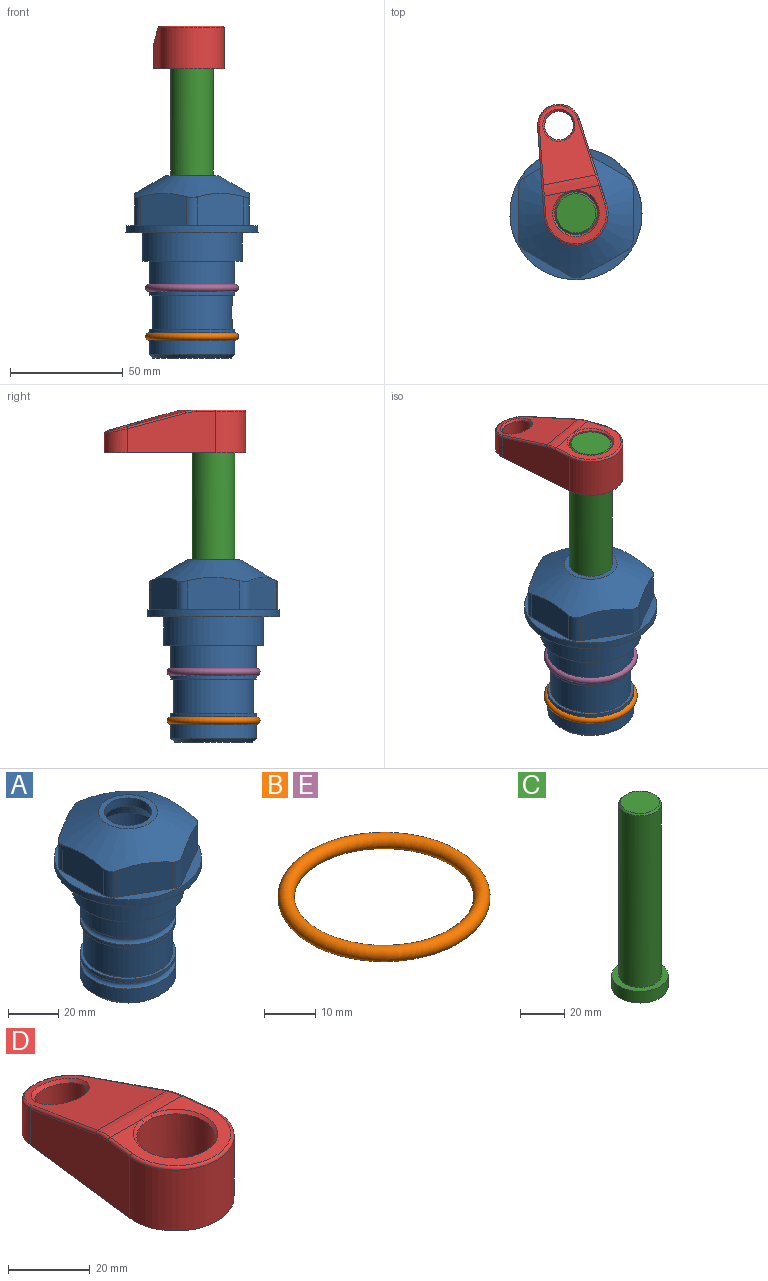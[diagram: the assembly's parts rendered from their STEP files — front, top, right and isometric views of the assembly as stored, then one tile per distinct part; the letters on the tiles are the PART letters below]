
ASSEMBLY  parts=5 mates=4
PART A: 36 faces, bbox 58.7x58.7x81 mm
  f0: cylinder r=17.78mm len=35.56mm, axis (0,0,1), area 1670.8mm2, adj f23,f24,f31
  f1: cylinder r=19.05mm len=38.1mm, axis (0,0,1), area 1191.9mm2, adj f26,f27,f30
  f2: plane 58.66x58.66mm, normal (0,0,-1), area 1150.6mm2, adj f3,f28
  f3: cylinder r=29.33mm len=58.66mm, axis (0,0,-1), area 585.1mm2, adj f2,f4
  f4: plane 58.66x58.66mm, normal (0,0,1), area 475.9mm2, adj f3,f5,f6,f7,f8,f9,f10,f11
  f5: plane 20.32x14.34mm, normal (-0.5,0.87,0), area 324.4mm2, adj f4,f15,f16,f17
  f6: plane 20.32x14.34mm, normal (0.5,0.87,0), area 324.4mm2, adj f4,f14,f15,f17
  f7: plane 23.48x14.34mm, normal (1,0,0), area 324.4mm2, adj f4,f13,f14,f17
  f8: plane 20.32x14.34mm, normal (0.5,-0.87,0), area 324.4mm2, adj f4,f12,f13,f17
  f9: plane 20.32x14.34mm, normal (-0.5,-0.87,0), area 324.4mm2, adj f4,f11,f12,f17
  f10: plane 23.48x14.34mm, normal (-1,0,0), area 324.4mm2, adj f4,f11,f16,f17
  f11: cylinder r=5.08mm len=12.85mm, axis (0,0,-1), area 67.2mm2, adj f4,f9,f10,f17
  f12: cylinder r=5.08mm len=12.85mm, axis (0,0,-1), area 67.2mm2, adj f4,f8,f9,f17
  f13: cylinder r=5.08mm len=12.85mm, axis (0,0,-1), area 67.2mm2, adj f4,f7,f8,f17
  f14: cylinder r=5.08mm len=12.85mm, axis (0,0,-1), area 67.2mm2, adj f4,f6,f7,f17
  f15: cylinder r=5.08mm len=12.85mm, axis (0,0,-1), area 67.2mm2, adj f4,f5,f6,f17
  f16: cylinder r=5.08mm len=12.85mm, axis (0,0,-1), area 67.2mm2, adj f4,f5,f10,f17
  f17: cone r=11.73mm half-angle=60deg, axis (0,0,-1), area 2071.8mm2, adj f5,f6,f7,f8,f9,f10,f11,f12
  f18: plane 23.46x23.46mm, normal (0,0,1), area 147.4mm2, adj f17,f35
  f19: plane 34.93x34.93mm, normal (0,0,-1), area 958mm2, adj f29
  f20: cylinder r=19.05mm len=38.1mm, axis (0,0,1), area 760.1mm2, adj f21,f29
  f21: torus R=19.05mm, axis (0,0,1), area 565.3mm2, adj f20,f22
  f22: cylinder r=19.05mm len=38.1mm, axis (0,0,1), area 190mm2, adj f21,f23
  f23: plane 38.1x38.1mm, normal (0,0,1), area 146.9mm2, adj f0,f22
  f24: plane 38.1x38.1mm, normal (0,0,-1), area 146.9mm2, adj f0,f25
  f25: cylinder r=19.05mm len=38.1mm, axis (0,0,1), area 190mm2, adj f24,f26
  f26: torus R=19.05mm, axis (0,0,1), area 565.3mm2, adj f1,f25
  f27: plane 44.45x44.45mm, normal (0,0,-1), area 411.7mm2, adj f1,f28
  f28: cylinder r=22.23mm len=44.45mm, axis (0,0,1), area 1773.5mm2, adj f2,f27
  f29: cone r=19.05mm half-angle=45deg, axis (0,0,1), area 257.5mm2, adj f19,f20
  f30: cylinder r=3.17mm len=6.75mm, axis (-1,0,0), area 128mm2, adj f1,f33
  f31: cylinder r=3.17mm len=6.35mm, axis (-1,0,0), area 102.5mm2, adj f0,f33
  f32: plane 25.4x25.4mm, normal (0,0,1), area 506.7mm2, adj f33
  f33: cylinder r=12.7mm len=66.42mm, axis (0,0,-1), area 5236.2mm2, adj f30,f31,f32,f34
  f34: cone r=9.53mm half-angle=30deg, axis (0,0,-1), area 443.4mm2, adj f33,f35
  f35: cylinder r=9.53mm len=19.05mm, axis (0,0,-1), area 240.9mm2, adj f18,f34
PART B: 1 faces, bbox 44.7x44.7x3.2 mm
  f0: torus R=19.05mm, axis (0,0,1), area 1193.9mm2
PART C: 6 faces, bbox 25.4x25.4x101.6 mm
  f0: plane 17.46x17.46mm, normal (0,0,1), area 239.5mm2, adj f5
  f1: plane 25.4x25.4mm, normal (0,0,-1), area 506.7mm2, adj f2
  f2: cylinder r=12.7mm len=25.4mm, axis (0,0,1), area 506.7mm2, adj f1,f3
  f3: plane 25.4x25.4mm, normal (0,0,1), area 221.7mm2, adj f2,f4
  f4: cylinder r=9.53mm len=94.46mm, axis (0,0,1), area 5653mm2, adj f3,f5
  f5: cone r=8.73mm half-angle=45deg, axis (0,0,-1), area 64.4mm2, adj f0,f4
PART D: 31 faces, bbox 31.7x65.5x19.8 mm
  f0: plane 39.12x18.26mm, normal (0.99,0.12,0), area 612.2mm2, adj f1,f4,f7,f11,f13,f15
  f1: cylinder r=9.53mm len=18.91mm, axis (0,0,-1), area 296.1mm2, adj f0,f2,f7,f17
  f2: plane 39.12x18.26mm, normal (-0.99,0.12,0), area 612.2mm2, adj f1,f4,f7,f12,f14,f16
  f3: cylinder r=6.35mm len=12.7mm, axis (0,0,-1), area 362.4mm2, adj f7,f18
  f4: cylinder r=14.29mm len=28.58mm, axis (0,0,-1), area 882.2mm2, adj f0,f2,f7,f10
  f5: cylinder r=9.53mm len=19.05mm, axis (0,0,-1), area 1092.6mm2, adj f7,f19,f20
  f6: plane 26.99x23.69mm, normal (0,0,1), area 216.2mm2, adj f9,f10,f11,f12,f19
  f7: plane 63.5x28.58mm, normal (0,0,-1), area 661.8mm2, adj f0,f1,f2,f3,f4,f5,f22,f23
  f8: plane 33.52x23.6mm, normal (0,0.26,0.97), area 486mm2, adj f9,f15,f16,f17,f18
  f9: cylinder r=19.05mm len=24.72mm, axis (1,0,0), area 120.4mm2, adj f6,f8,f13,f14,f20
  f10: torus R=13.49mm, axis (0,0,1), area 59mm2, adj f4,f6,f11,f12
  f11: cylinder r=0.79mm len=8.67mm, axis (0.12,-0.99,0), area 10.8mm2, adj f0,f6,f10,f13
  f12: cylinder r=0.79mm len=8.67mm, axis (0.12,0.99,0), area 10.8mm2, adj f2,f6,f10,f14
  f13: bspline ~4.95x1.42mm, area 6.1mm2, adj f0,f9,f11,f15
  f14: bspline ~4.95x1.42mm, area 6.1mm2, adj f2,f9,f12,f16
  f15: cylinder r=0.79mm len=25.95mm, axis (0.12,-0.96,0.26), area 32.9mm2, adj f0,f8,f13,f17
  f16: cylinder r=0.79mm len=25.95mm, axis (0.12,0.96,-0.26), area 32.9mm2, adj f2,f8,f14,f17
  f17: bspline ~18.91x8.38mm, area 30mm2, adj f1,f8,f15,f16
  f18: bspline ~14.29x14.29mm, area 48.3mm2, adj f3,f8
  f19: cone r=9.53mm half-angle=45deg, axis (0,0,1), area 66.5mm2, adj f5,f6,f20
  f20: bspline ~3.22x0.96mm, area 3.5mm2, adj f5,f9,f19
  f21: plane 2.75x2.72mm, normal (0,0,-1), area 2.9mm2, adj f23,f25,f28
  f22: plane 23.05x15.88mm, normal (-0.99,-0.12,0), area 323.6mm2, adj f7,f25,f26,f27,f28,f29
  f23: plane 23.05x15.88mm, normal (0.99,-0.12,0), area 323.6mm2, adj f7,f21,f25,f27,f28,f30
  f24: cylinder r=9.53mm len=10.69mm, axis (0,0,-1), area 114.7mm2, adj f7,f27,f29,f30
  f25: cylinder r=12.7mm len=20.59mm, axis (0,0,-1), area 381.1mm2, adj f7,f21,f22,f23,f26,f28
  f26: plane 2.75x2.72mm, normal (0,0,-1), area 2.9mm2, adj f22,f25,f28
  f27: plane 19.72x18.37mm, normal (0,-0.26,-0.97), area 291.8mm2, adj f22,f23,f24,f28,f29,f30
  f28: cylinder r=15.88mm len=19.92mm, axis (1,0,0), area 54.8mm2, adj f21,f22,f23,f25,f26,f27
  f29: cylinder r=1.59mm len=11mm, axis (0,0,-1), area 34.7mm2, adj f7,f22,f24,f27
  f30: cylinder r=1.59mm len=11mm, axis (0,0,-1), area 34.7mm2, adj f7,f23,f24,f27
PART E: same geometry as B
PLACE A at identity fixed
PLACE B t=(0,0,-21.59)mm
PLACE C rot(axis=(0,0,1),11deg) t=(0,0,27.55)mm
PLACE D rot(axis=(0,0,1),11deg) t=(0,0,28.35)mm
PLACE E at identity
MATE fastened B.f0 <-> A.f0  axis (0,0,1) through (0,0,-46.1)mm
MATE cylindrical C.f2 <-> A.f0  axis (0,0,-1) through (0,0,-10.55)mm
MATE fastened D.f4 <-> C.f2  axis (0,0,-1) through (0,0,91.05)mm
MATE fastened E.f0 <-> A.f0  axis (0,0,1) through (0,0,-24.51)mm
